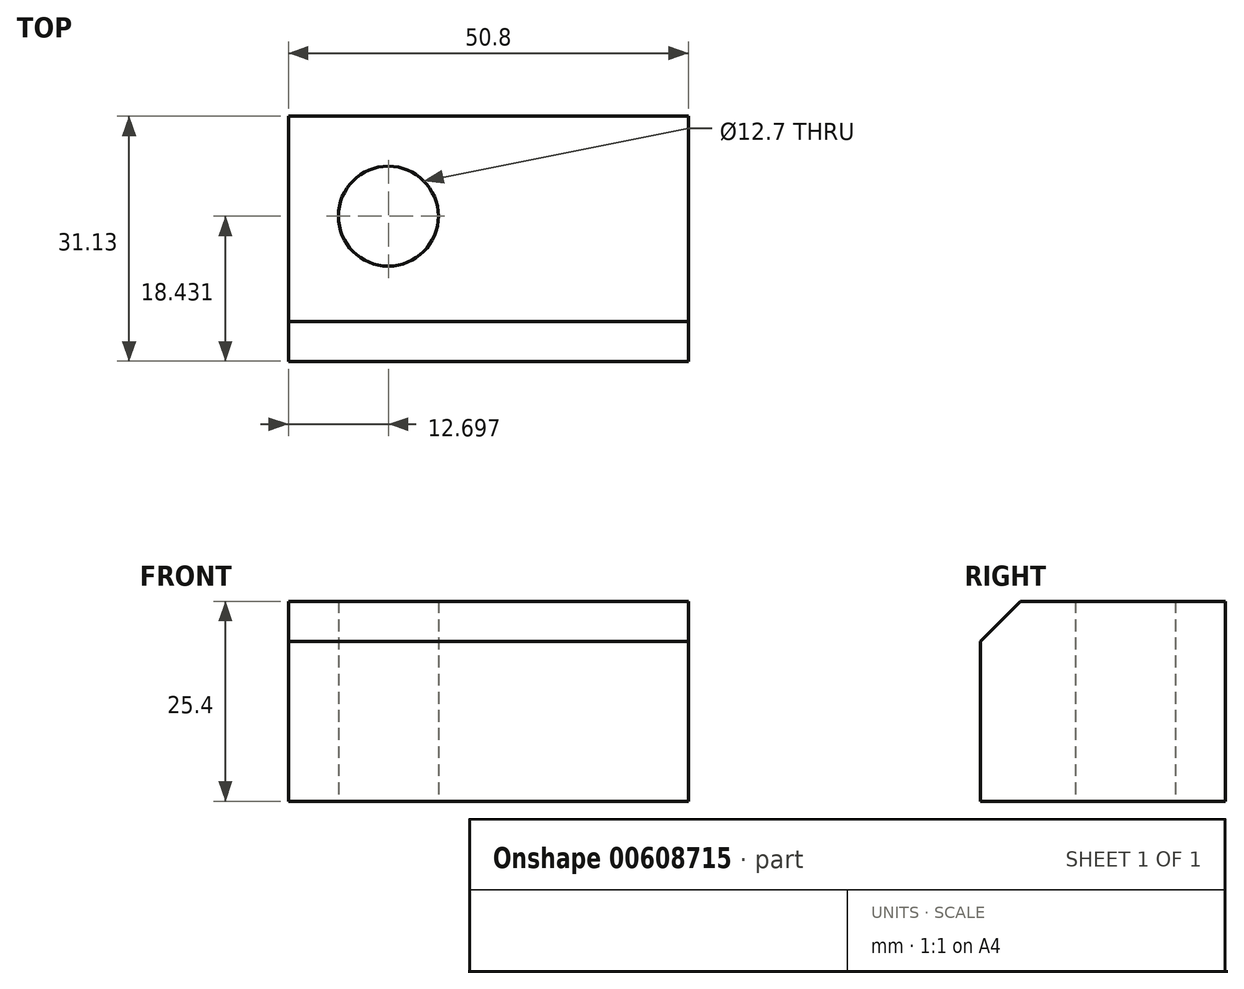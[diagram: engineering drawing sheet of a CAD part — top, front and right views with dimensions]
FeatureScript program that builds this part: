
annotation { "Feature Type Name" : "Feature", "Feature Type Description" : "" }
export const myFeature = defineFeature(function(context is Context, id is Id, definition is map)
    precondition{}
    {
        {
            var Q0;
            Q0=qCreatedBy(makeId("Top.planeOp"),FACE);
            var sketch = newSketch(context, id + "F0", { "sketchPlane" : qUnion([Q0])});
            skLineSegment(sketch, "E0.bottom", {"start": v(-40.6, 5.4) * mm, "end": v(10.2, 5.4) * mm});
            skLineSegment(sketch, "E0.top", {"start": v(-40.6, -25.73) * mm, "end": v(10.2, -25.73) * mm});
            skLineSegment(sketch, "E0.left", {"start": v(-40.6, 5.4) * mm, "end": v(-40.6, -25.73) * mm});
            skLineSegment(sketch, "E0.right", {"start": v(10.2, 5.4) * mm, "end": v(10.2, -25.73) * mm});
            skCircle(sketch, "E1", {"center": v(-27.9, -7.3) * mm, "radius": 6.35 * mm});
            skSolve(sketch);
        }
        {
            var Q0;
            Q0 = qSketchRegion(id + "F0", true);
            extrude(context, id + "F1", {"entities" : qUnion([Q0]), "depth" : 25.4 * mm, "offsetDistance" : 25.4 * mm});
        }
        {
            var Q0;
            Q0=makeQuery(id+"F1.opExtrude","CAP_EDGE",EDGE,{"disambiguationData":[OSD([sQuery(id+"F0.wireOp",EDGE,"E0.top")])],"isStart":false});
            chamfer(context, id + "F2", {"entities" : qUnion([Q0]), "width" : 5.08 * mm, "tangentPropagation" : true});
        }
    });
